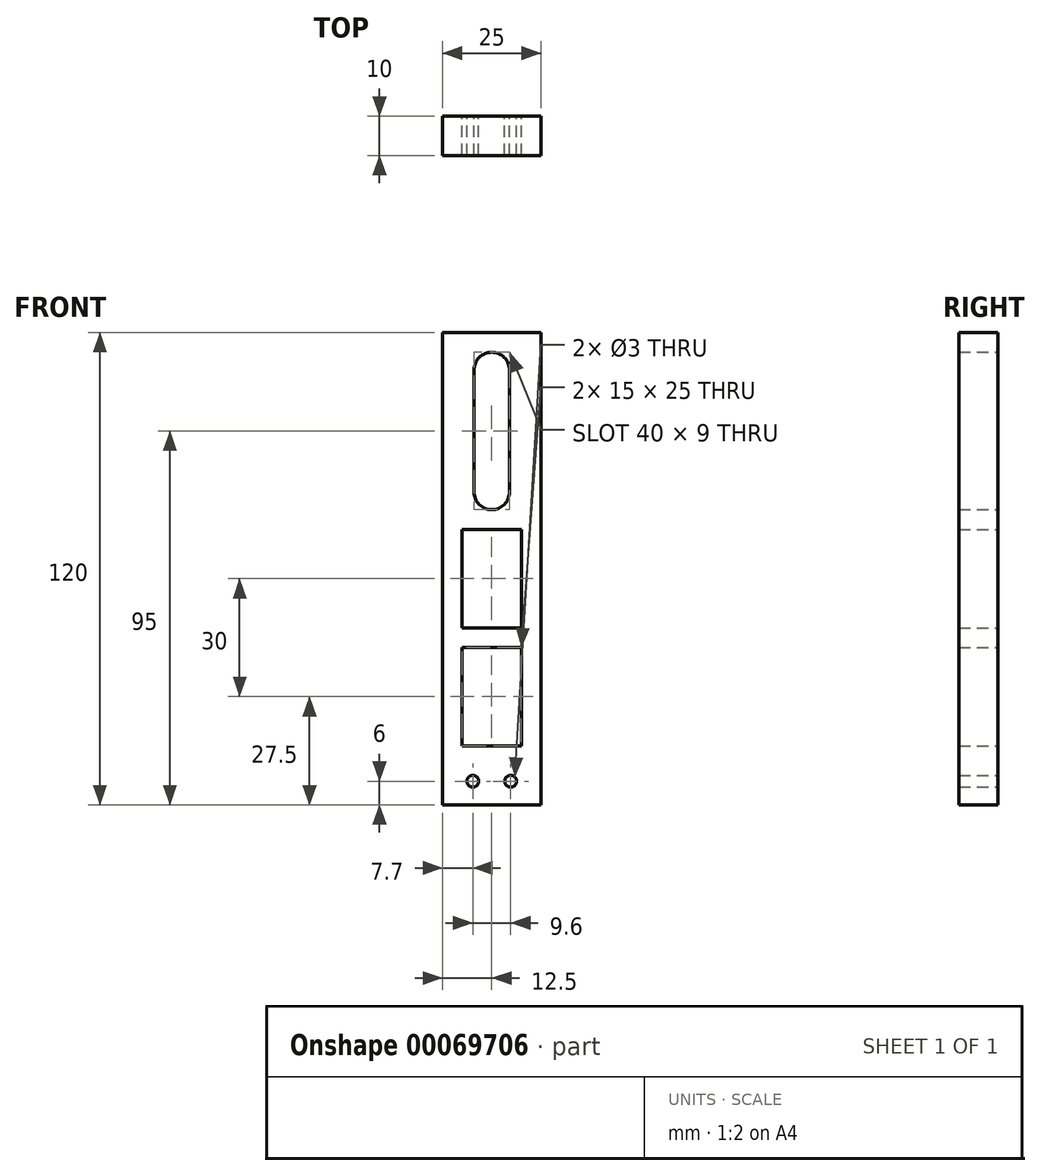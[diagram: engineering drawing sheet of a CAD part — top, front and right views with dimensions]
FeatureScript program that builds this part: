
annotation { "Feature Type Name" : "Feature", "Feature Type Description" : "" }
export const myFeature = defineFeature(function(context is Context, id is Id, definition is map)
    precondition{}
    {
        {
            var Q0;
            Q0=qCreatedBy(makeId("Front.planeOp"),FACE);
            var sketch = newSketch(context, id + "F0", { "sketchPlane" : qUnion([Q0])});
            skLineSegment(sketch, "E0.bottom", {"start": v(0, 0) * mm, "end": v(25, 0) * mm});
            skLineSegment(sketch, "E0.left", {"start": v(0, 0) * mm, "end": v(0, 120) * mm});
            skLineSegment(sketch, "E0.right", {"start": v(25, 0) * mm, "end": v(25, 120) * mm});
            skCircle(sketch, "E1", {"center": v(7.7, 6) * mm, "radius": 1.5 * mm});
            skCircle(sketch, "E2", {"center": v(17.3, 6) * mm, "radius": 1.5 * mm});
            skLineSegment(sketch, "E3", {"start": v(7.7, 6) * mm, "end": v(17.3, 6) * mm, "construction": true});
            skLineSegment(sketch, "E4", {"start": v(12.5, 0) * mm, "end": v(12.5, 6) * mm, "construction": true});
            skLineSegment(sketch, "E5", {"start": v(0, 120) * mm, "end": v(25, 120) * mm});
            skLineSegment(sketch, "E6.bottom", {"start": v(12.5, 115) * mm, "end": v(12.5, 115) * mm});
            skLineSegment(sketch, "E6.top", {"start": v(12.5, 75) * mm, "end": v(12.5, 75) * mm});
            skLineSegment(sketch, "E6.left", {"start": v(8, 110.5) * mm, "end": v(8, 79.5) * mm});
            skLineSegment(sketch, "E6.right", {"start": v(17, 110.5) * mm, "end": v(17, 79.5) * mm});
            skLineSegment(sketch, "E7", {"start": v(12.5, 115) * mm, "end": v(12.5, 120) * mm, "construction": true});
            skPoint(sketch, "E8.visualSharp", {"position": v(8, 115) * mm});
            skArc(sketch, "E8.filletArc", {"start": v(12.5, 115) * mm, "mid": v(9.32, 113.68) * mm, "end": v(8, 110.5) * mm});
            skPoint(sketch, "E9.visualSharp", {"position": v(17, 115) * mm});
            skArc(sketch, "E9.filletArc", {"start": v(17, 110.5) * mm, "mid": v(15.68, 113.68) * mm, "end": v(12.5, 115) * mm});
            skPoint(sketch, "E10.visualSharp", {"position": v(17, 75) * mm});
            skArc(sketch, "E10.filletArc", {"start": v(12.5, 75) * mm, "mid": v(15.68, 76.32) * mm, "end": v(17, 79.5) * mm});
            skPoint(sketch, "E11.visualSharp", {"position": v(8, 75) * mm});
            skArc(sketch, "E11.filletArc", {"start": v(8, 79.5) * mm, "mid": v(9.32, 76.32) * mm, "end": v(12.5, 75) * mm});
            skLineSegment(sketch, "E12.bottom", {"start": v(5, 70) * mm, "end": v(20, 70) * mm});
            skLineSegment(sketch, "E12.top", {"start": v(5, 45) * mm, "end": v(20, 45) * mm});
            skLineSegment(sketch, "E12.left", {"start": v(5, 70) * mm, "end": v(5, 45) * mm});
            skLineSegment(sketch, "E12.right", {"start": v(20, 70) * mm, "end": v(20, 45) * mm});
            skLineSegment(sketch, "E13.1.0.0", {"start": v(5, 15) * mm, "end": v(20, 15) * mm});
            skLineSegment(sketch, "E13.1.0.1", {"start": v(20, 40) * mm, "end": v(20, 15) * mm});
            skLineSegment(sketch, "E13.1.0.2", {"start": v(5, 40) * mm, "end": v(20, 40) * mm});
            skLineSegment(sketch, "E13.1.0.3", {"start": v(5, 40) * mm, "end": v(5, 15) * mm});
            skLineSegment(sketch, "E13.direction1", {"start": v(5, 70) * mm, "end": v(5, 40) * mm, "construction": true});
            skSolve(sketch);
        }
        {
            var Q0;
            Q0 = qSketchRegion(id + "F0", true);
            extrude(context, id + "F1", {"entities" : qUnion([Q0]), "depth" : 10 * mm, "offsetDistance" : 25 * mm});
        }
    });
